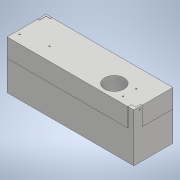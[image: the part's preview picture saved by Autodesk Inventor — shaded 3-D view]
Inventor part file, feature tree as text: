
AUTODESK INVENTOR PART (.ipt)
format: ipt  version: 2020 (Build 240168000, 168)  size: 387,072 bytes
history: native  units: mm
features: sketch x17, other x13, extrude x11, hole x5
ambient origin geometry x8: Origin, YZ Plane, XZ Plane, XY Plane, X Axis, Y Axis, Z Axis, Center Point
bodies: Body1 (feature_tree), Body2 (feature_tree)
feature tree (46):
  other  "Твердое тело1"
  extrude  "Выдавливание1"  Depth=152.5mm
  extrude  "Выдавливание2"  Depth=47.0mm
  extrude  "Выдавливание4"  Depth=30.0mm TaperAngle=0.0deg
  extrude  "Выдавливание7"  Depth=24.0mm
  extrude  "Выдавливание8"  Depth=3.0mm TaperAngle=0.0deg
  extrude  "Выдавливание9"  Depth=2.0mm
  other  "РабПлоскость1"
  other  "Разделение1"
  extrude  "Выдавливание26"  Depth=20.0mm
  extrude  "Выдавливание27"  Depth=3.0mm TaperAngle=0.0deg
  extrude  "Выдавливание28"  Depth=23.5mm
  sketch  "Эскиз24"
  hole  "Отверстие1"  [1 undecoded]
  extrude  "Выдавливание29"  Depth=25.0mm TaperAngle=0.0deg
  extrude  "Выдавливание30"  Depth=2.7mm
  hole  "Отверстие2"  [1 undecoded]
  hole  "Отверстие3"  [1 undecoded]
  hole  "Отверстие4"  [1 undecoded]
  hole  "Отверстие5"  [1 undecoded]
  sketch  "Эскиз1"
  sketch  "Эскиз2"
  sketch  "Эскиз3"
  sketch  "Эскиз4"
  sketch  "Эскиз6"
  sketch  "Эскиз7"
  sketch  "Эскиз20"
  sketch  "Эскиз21"
  sketch  "Эскиз22"
  sketch  "Эскиз23"
  sketch  "Эскиз25"
  sketch  "Эскиз26"
  sketch  "Эскиз27"
  sketch  "Эскиз28"
  sketch  "Эскиз29"
  sketch  "Эскиз30"
  other  "Проецирование ребер1"
  other  "Проецирование ребер3"
  other  "Твердое тело2"
  other  "Твердое тело3"
  other  "Проецирование ребер7"
  other  "Проецирование ребер8"
  other  "Проецирование ребер9"
  other  "Проецирование ребер10"
  other  "Проецирование ребер11"
  other  "Проецирование ребер12"
note: 5 required parameter values undecoded (feature->parameter linkage not recoverable at this tier; creation-order binding heuristic only, values carry confidence <= 0.55)
